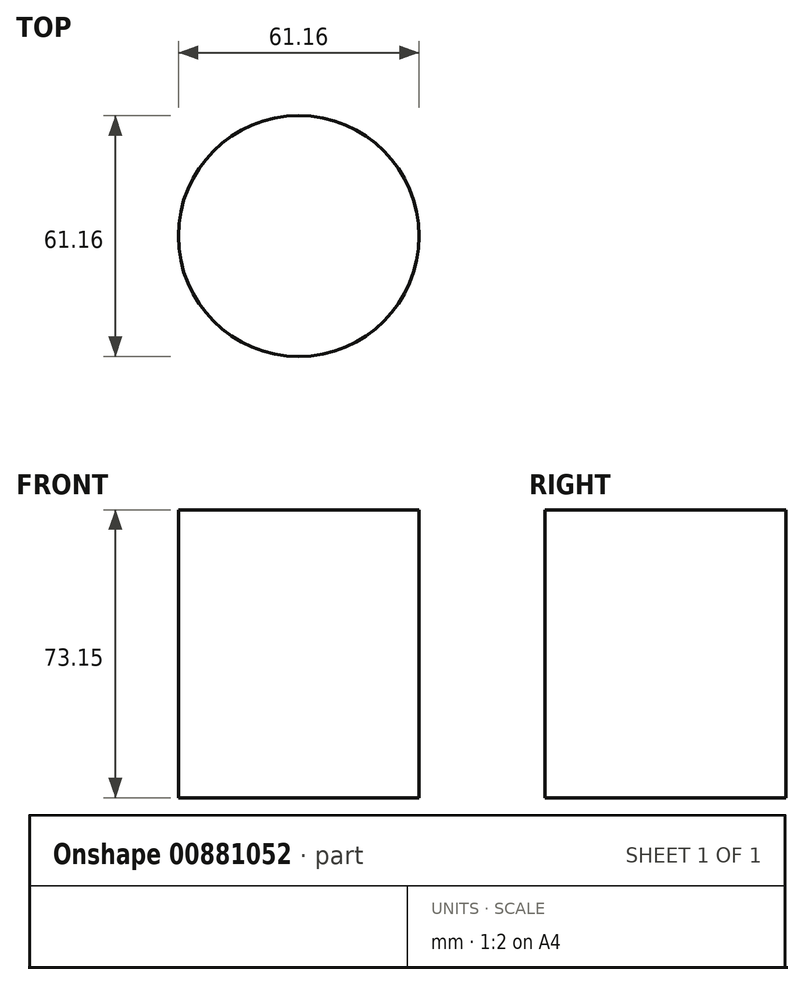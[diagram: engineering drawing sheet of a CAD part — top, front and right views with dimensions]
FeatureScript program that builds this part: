
annotation { "Feature Type Name" : "Feature", "Feature Type Description" : "" }
export const myFeature = defineFeature(function(context is Context, id is Id, definition is map)
    precondition{}
    {
        {
            var Q0;
            Q0=qCreatedBy(makeId("Top.planeOp"),FACE);
            var sketch = newSketch(context, id + "F0", { "sketchPlane" : qUnion([Q0])});
            skCircle(sketch, "E0", {"center": v(0, 0) * mm, "radius": 30.58 * mm});
            skSolve(sketch);
        }
        {
            var Q0;
            Q0=makeQuery(id+"F0.imprint","IMPRINT",FACE,{"disambiguationData":[TD([[makeQuery(id+"F0.imprint","IMPRINT",EDGE,{"derivedFrom":sQuery(id+"F0.wireOp",EDGE,"E0")}),1.0]])]});
            extrude(context, id + "F1", {"entities" : qUnion([Q0]), "depth" : 73.15 * mm, "offsetDistance" : 25.4 * mm});
        }
    });
